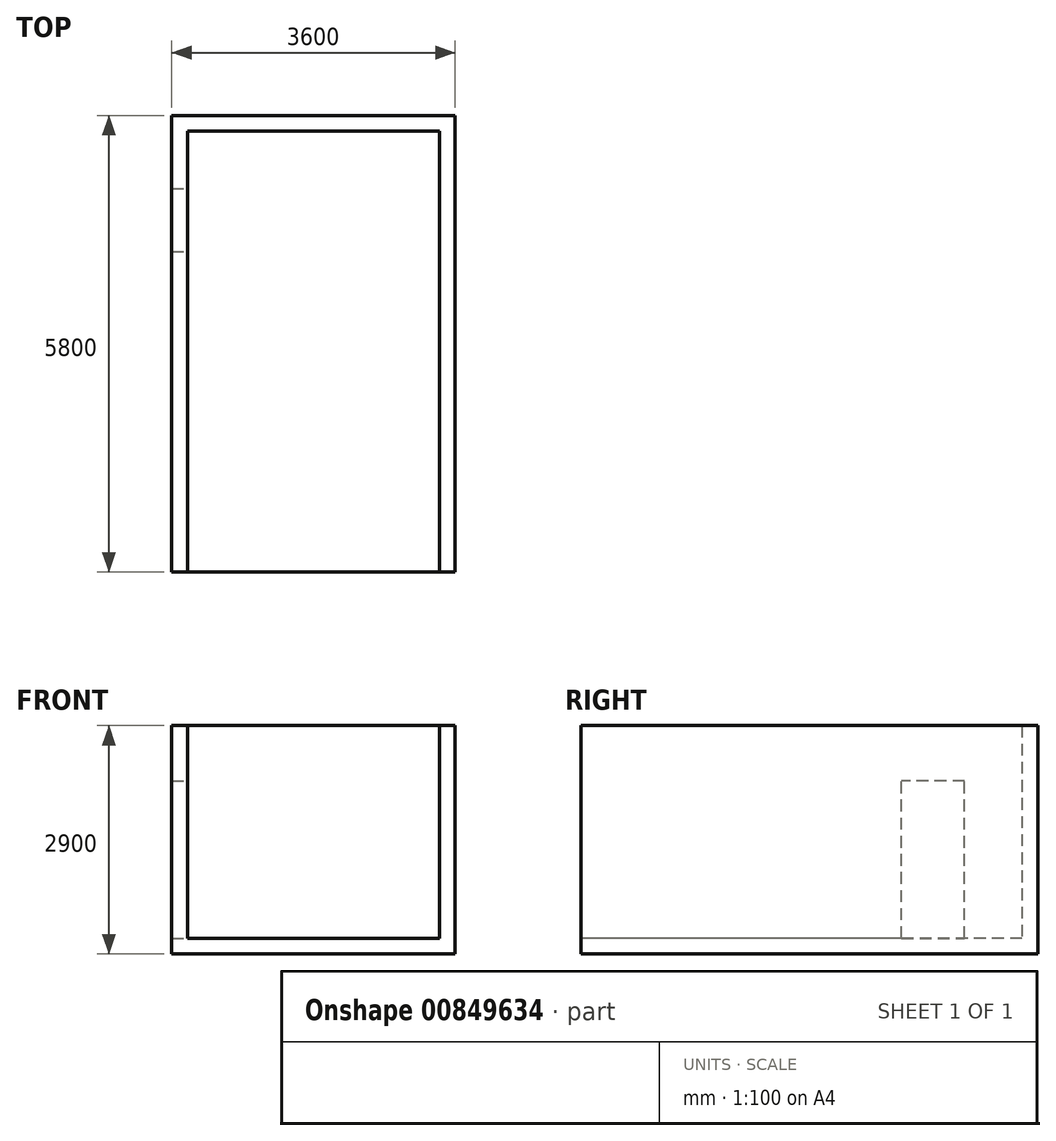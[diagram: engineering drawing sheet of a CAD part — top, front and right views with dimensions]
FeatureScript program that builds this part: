
annotation { "Feature Type Name" : "Feature", "Feature Type Description" : "" }
export const myFeature = defineFeature(function(context is Context, id is Id, definition is map)
    precondition{}
    {
        {
            var Q0;
            Q0=qCreatedBy(makeId("Top.planeOp"),FACE);
            var sketch = newSketch(context, id + "F0", { "sketchPlane" : qUnion([Q0])});
            skLineSegment(sketch, "E0.bottom", {"start": v(-1800, 2900) * mm, "end": v(1800, 2900) * mm});
            skLineSegment(sketch, "E0.top", {"start": v(-1800, -2900) * mm, "end": v(1800, -2900) * mm});
            skLineSegment(sketch, "E0.left", {"start": v(-1800, 2900) * mm, "end": v(-1800, -2900) * mm});
            skLineSegment(sketch, "E0.right", {"start": v(1800, 2900) * mm, "end": v(1800, -2900) * mm});
            skSolve(sketch);
        }
        {
            var Q0;
            Q0=makeQuery(id+"F0.imprint","IMPRINT",FACE,{"disambiguationData":[TD([[makeQuery(id+"F0.imprint","IMPRINT",EDGE,{"derivedFrom":sQuery(id+"F0.wireOp",EDGE,"E0.bottom")}),-1.0]])]});
            extrude(context, id + "F1", {"entities" : qUnion([Q0]), "depth" : 2900 * mm, "offsetDistance" : 25 * mm});
        }
        {
            var Q0;
            Q0=makeQuery(id+"F1.opExtrude","SWEPT_FACE",FACE,{"disambiguationData":[OSD([sQuery(id+"F0.wireOp",EDGE,"E0.top")])]});
            var sketch = newSketch(context, id + "F2", { "sketchPlane" : qUnion([Q0])});
            skLineSegment(sketch, "E1.0", {"start": v(-1600, 200) * mm, "end": v(1600, 200) * mm});
            skLineSegment(sketch, "E1.1", {"start": v(-1600, 2900) * mm, "end": v(-1600, 200) * mm});
            skLineSegment(sketch, "E1.3", {"start": v(1600, 200) * mm, "end": v(1600, 2900) * mm});
            skSolve(sketch);
        }
        {
            var Q0;
            Q0=makeQuery(id+"F2.imprint","IMPRINT",FACE,{"disambiguationData":[TD([[makeQuery(id+"F2.imprint","IMPRINT",EDGE,{"derivedFrom":sQuery(id+"F2.wireOp",EDGE,"E1.0")}),1.0]])]});
            extrude(context, id + "F3", {"entities" : qUnion([Q0]), "operationType" : NewBodyOperationType.REMOVE, "oppositeDirection" : true, "depth" : 5600 * mm, "offsetDistance" : 25 * mm});
        }
        {
            var Q0;
            Q0=makeQuery(id+"F3.boolean.opBoolean","COPY",FACE,{"derivedFrom":makeQuery(id+"F3.opExtrude","SWEPT_FACE",FACE,{"disambiguationData":[OSD([sQuery(id+"F2.wireOp",EDGE,"E1.1")])]})});
            var sketch = newSketch(context, id + "F4", { "sketchPlane" : qUnion([Q0])});
            skLineSegment(sketch, "E2.bottom", {"start": v(1970, 200) * mm, "end": v(1170, 200) * mm});
            skLineSegment(sketch, "E2.top", {"start": v(1970, 2200) * mm, "end": v(1170, 2200) * mm});
            skLineSegment(sketch, "E2.left", {"start": v(1970, 200) * mm, "end": v(1970, 2200) * mm});
            skLineSegment(sketch, "E2.right", {"start": v(1170, 200) * mm, "end": v(1170, 2200) * mm});
            skSolve(sketch);
        }
        {
            var Q0;
            Q0=makeQuery(id+"F4.imprint","IMPRINT",FACE,{"disambiguationData":[TD([[makeQuery(id+"F4.imprint","IMPRINT",EDGE,{"derivedFrom":sQuery(id+"F4.wireOp",EDGE,"E2.bottom")}),-1.0]])]});
            extrude(context, id + "F5", {"entities" : qUnion([Q0]), "operationType" : NewBodyOperationType.REMOVE, "endBound" : BoundingType.UP_TO_NEXT, "oppositeDirection" : true, "depth" : 25 * mm, "offsetDistance" : 25 * mm});
        }
    });
